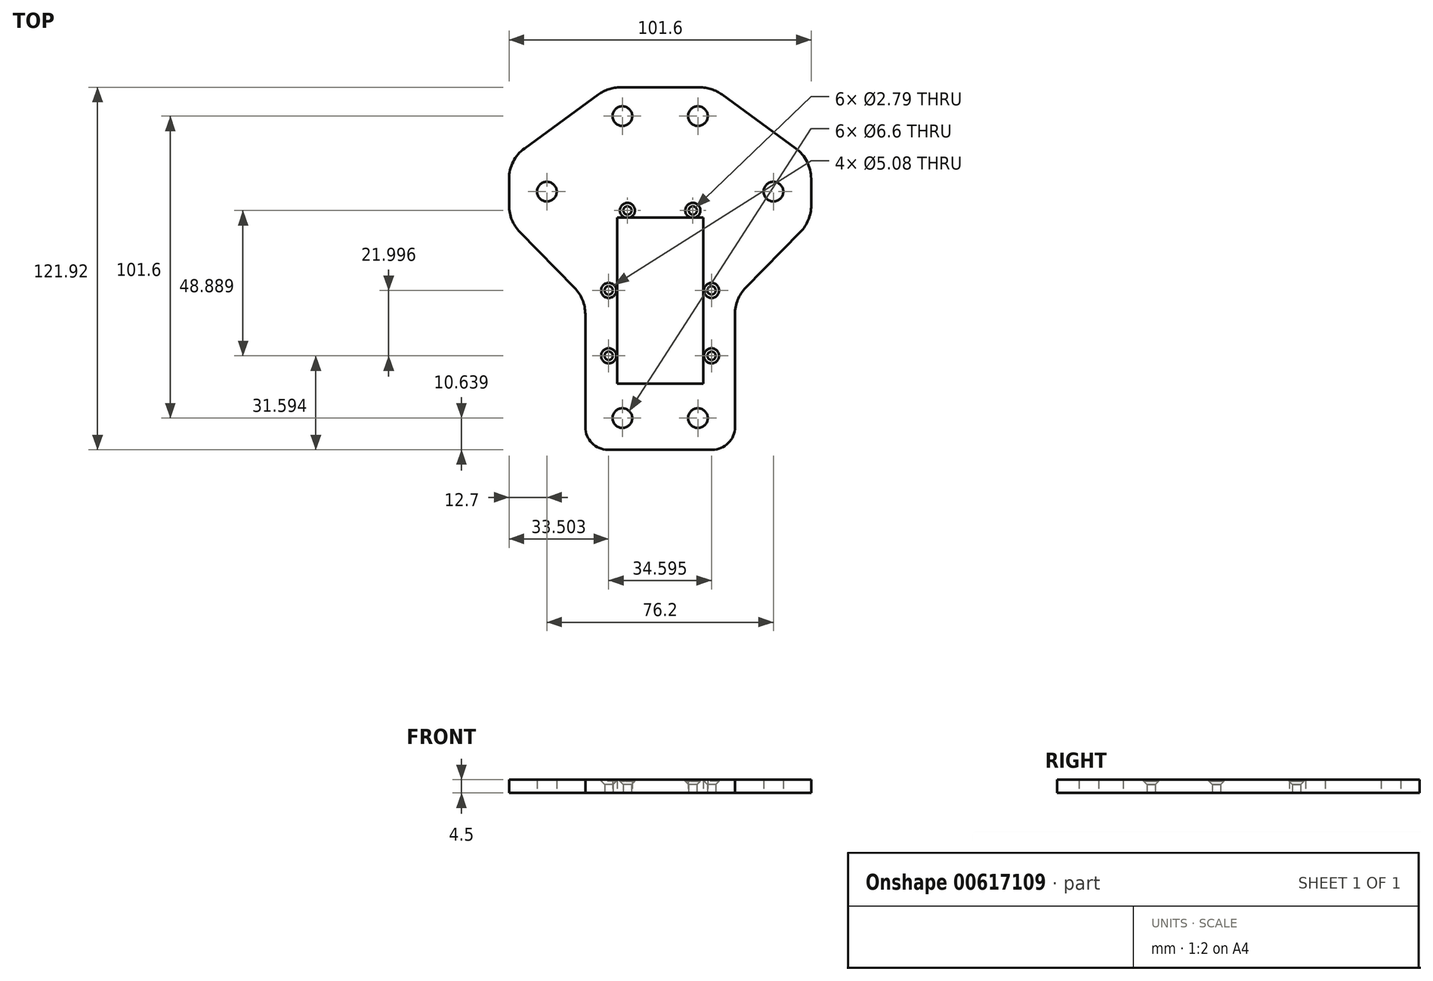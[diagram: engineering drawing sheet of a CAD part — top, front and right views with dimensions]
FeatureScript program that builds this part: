
annotation { "Feature Type Name" : "Feature", "Feature Type Description" : "" }
export const myFeature = defineFeature(function(context is Context, id is Id, definition is map)
    precondition{}
    {
        {
            var Q0;
            Q0=qCreatedBy(makeId("Top.planeOp"),FACE);
            var sketch = newSketch(context, id + "F0", { "sketchPlane" : qUnion([Q0])});
            skLineSegment(sketch, "E0", {"start": v(-13.32, 71.76) * mm, "end": v(0, 71.76) * mm});
            skLineSegment(sketch, "E1", {"start": v(-20.8, 69.31) * mm, "end": v(-45.59, 51.23) * mm});
            skLineSegment(sketch, "E2", {"start": v(-50.8, 40.97) * mm, "end": v(-50.8, 31.97) * mm});
            skLineSegment(sketch, "E3", {"start": v(-47.17, 23.08) * mm, "end": v(-28.8, 4.34) * mm});
            skLineSegment(sketch, "E4", {"start": v(-25.17, -4.55) * mm, "end": v(-25.17, -42.54) * mm});
            skLineSegment(sketch, "E5", {"start": v(-17.55, -50.16) * mm, "end": v(0, -50.16) * mm});
            skLineSegment(sketch, "E6", {"start": v(0, -50.16) * mm, "end": v(0, -27.94) * mm});
            skLineSegment(sketch, "E7", {"start": v(0, -27.94) * mm, "end": v(-14.5, -27.94) * mm});
            skLineSegment(sketch, "E8", {"start": v(-14.5, -27.94) * mm, "end": v(-14.5, 27.94) * mm});
            skLineSegment(sketch, "E9", {"start": v(-14.5, 27.94) * mm, "end": v(0, 27.94) * mm});
            skLineSegment(sketch, "E10", {"start": v(0, 27.94) * mm, "end": v(0, 71.76) * mm});
            skPoint(sketch, "E11.visualSharp", {"position": v(-17.46, 71.76) * mm});
            skArc(sketch, "E11.filletArc", {"start": v(-13.32, 71.76) * mm, "mid": v(-17.26, 71.13) * mm, "end": v(-20.8, 69.31) * mm});
            skPoint(sketch, "E12.visualSharp", {"position": v(-50.8, 47.42) * mm});
            skArc(sketch, "E12.filletArc", {"start": v(-45.59, 51.23) * mm, "mid": v(-49.42, 46.72) * mm, "end": v(-50.8, 40.97) * mm});
            skPoint(sketch, "E13.visualSharp", {"position": v(-50.8, 26.78) * mm});
            skArc(sketch, "E13.filletArc", {"start": v(-50.8, 31.97) * mm, "mid": v(-49.86, 27.17) * mm, "end": v(-47.17, 23.08) * mm});
            skPoint(sketch, "E14.visualSharp", {"position": v(-25.17, 0.64) * mm});
            skArc(sketch, "E14.filletArc", {"start": v(-25.17, -4.55) * mm, "mid": v(-26.11, 0.25) * mm, "end": v(-28.8, 4.34) * mm});
            skPoint(sketch, "E15.visualSharp", {"position": v(-25.17, -50.16) * mm});
            skArc(sketch, "E15.filletArc", {"start": v(-25.17, -42.54) * mm, "mid": v(-22.94, -47.93) * mm, "end": v(-17.55, -50.16) * mm});
            skLineSegment(sketch, "E16", {"start": v(-12.7, 83.28) * mm, "end": v(-12.7, -82.95) * mm, "construction": true});
            skLineSegment(sketch, "E17", {"start": v(91.24, 62.08) * mm, "end": v(-114.1, 62.08) * mm, "construction": true});
            skLineSegment(sketch, "E18", {"start": v(85.27, 36.68) * mm, "end": v(-111.23, 36.68) * mm, "construction": true});
            skLineSegment(sketch, "E19", {"start": v(-95.95, -39.52) * mm, "end": v(84.27, -39.52) * mm, "construction": true});
            skLineSegment(sketch, "E20", {"start": v(-38.1, 82.08) * mm, "end": v(-38.1, -58.2) * mm, "construction": true});
            skCircle(sketch, "E21", {"center": v(-12.7, 62.08) * mm, "radius": 3.3 * mm});
            skCircle(sketch, "E22", {"center": v(-38.1, 36.68) * mm, "radius": 3.3 * mm});
            skCircle(sketch, "E23", {"center": v(-12.7, -39.52) * mm, "radius": 3.3 * mm});
            skCircle(sketch, "E24", {"center": v(-11, 30.32) * mm, "radius": 1.4 * mm});
            skCircle(sketch, "E25", {"center": v(-17.3, 3.43) * mm, "radius": 1.4 * mm});
            skCircle(sketch, "E26", {"center": v(-17.3, -18.57) * mm, "radius": 1.4 * mm});
            skSolve(sketch);
        }
        {
            var Q0;
            Q0=makeQuery(id+"F0.imprint","IMPRINT",FACE,{"disambiguationData":[TD([[makeQuery(id+"F0.imprint","IMPRINT",EDGE,{"derivedFrom":sQuery(id+"F0.wireOp",EDGE,"E0")}),-1.0]])]});
            extrude(context, id + "F1", {"entities" : qUnion([Q0]), "depth" : 4.5 * mm, "offsetDistance" : 25.4 * mm});
        }
        {
            var Q0;
            Q0=makeQuery(id+"F1.opExtrude","SWEPT_BODY",BODY,{"disambiguationData":[OSD([sQuery(id+"F0.wireOp",EDGE,"E0"),sQuery(id+"F0.wireOp",EDGE,"E1"),sQuery(id+"F0.wireOp",EDGE,"E2"),sQuery(id+"F0.wireOp",EDGE,"E3"),sQuery(id+"F0.wireOp",EDGE,"E4"),sQuery(id+"F0.wireOp",EDGE,"E5"),sQuery(id+"F0.wireOp",EDGE,"E6"),sQuery(id+"F0.wireOp",EDGE,"E7"),sQuery(id+"F0.wireOp",EDGE,"E8"),sQuery(id+"F0.wireOp",EDGE,"E9"),sQuery(id+"F0.wireOp",EDGE,"E10"),sQuery(id+"F0.wireOp",EDGE,"E11.filletArc"),sQuery(id+"F0.wireOp",EDGE,"E12.filletArc"),sQuery(id+"F0.wireOp",EDGE,"E13.filletArc"),sQuery(id+"F0.wireOp",EDGE,"E14.filletArc"),sQuery(id+"F0.wireOp",EDGE,"E15.filletArc"),sQuery(id+"F0.wireOp",EDGE,"E21"),sQuery(id+"F0.wireOp",EDGE,"E22"),sQuery(id+"F0.wireOp",EDGE,"E23"),sQuery(id+"F0.wireOp",EDGE,"E24"),sQuery(id+"F0.wireOp",EDGE,"E25"),sQuery(id+"F0.wireOp",EDGE,"E26")])]});
            var Q1;
            Q1=makeQuery(id+"F1.opExtrude","SWEPT_FACE",FACE,{"disambiguationData":[OSD([sQuery(id+"F0.wireOp",EDGE,"E10")])]});
            mirror(context, id + "F2", {"operationType" : NewBodyOperationType.ADD, "entities" : qUnion([Q0]), "mirrorPlane" : qUnion([Q1])});
        }
        {
            var Q0;
            {var subQ0=makeQuery(id+"F1.opExtrude","CAP_FACE",FACE,{"disambiguationData":[OSD([sQuery(id+"F0.wireOp",EDGE,"E0"),sQuery(id+"F0.wireOp",EDGE,"E1"),sQuery(id+"F0.wireOp",EDGE,"E2"),sQuery(id+"F0.wireOp",EDGE,"E3"),sQuery(id+"F0.wireOp",EDGE,"E4"),sQuery(id+"F0.wireOp",EDGE,"E5"),sQuery(id+"F0.wireOp",EDGE,"E6"),sQuery(id+"F0.wireOp",EDGE,"E7"),sQuery(id+"F0.wireOp",EDGE,"E8"),sQuery(id+"F0.wireOp",EDGE,"E9"),sQuery(id+"F0.wireOp",EDGE,"E10"),sQuery(id+"F0.wireOp",EDGE,"E11.filletArc"),sQuery(id+"F0.wireOp",EDGE,"E12.filletArc"),sQuery(id+"F0.wireOp",EDGE,"E13.filletArc"),sQuery(id+"F0.wireOp",EDGE,"E14.filletArc"),sQuery(id+"F0.wireOp",EDGE,"E15.filletArc"),sQuery(id+"F0.wireOp",EDGE,"E21"),sQuery(id+"F0.wireOp",EDGE,"E22"),sQuery(id+"F0.wireOp",EDGE,"E23"),sQuery(id+"F0.wireOp",EDGE,"E24"),sQuery(id+"F0.wireOp",EDGE,"E25"),sQuery(id+"F0.wireOp",EDGE,"E26")])],"isStart":false});Q0=makeQuery(id+"F2.boolean.opBoolean","MERGE",FACE,{"derivedFrom":[subQ0,makeQuery(id+"F2.opPattern","COPY",FACE,{"derivedFrom":subQ0,"instanceName":"1"})]});}
            var sketch = newSketch(context, id + "F3", { "sketchPlane" : qUnion([Q0])});
            skCircle(sketch, "E27", {"center": v(-11, 30.32) * mm, "radius": 2.54 * mm});
            skCircle(sketch, "E28", {"center": v(-17.3, 3.43) * mm, "radius": 2.54 * mm});
            skCircle(sketch, "E29", {"center": v(-17.3, -18.57) * mm, "radius": 2.54 * mm});
            skCircle(sketch, "E30", {"center": v(11, 30.32) * mm, "radius": 2.54 * mm});
            skCircle(sketch, "E31", {"center": v(17.3, 3.43) * mm, "radius": 2.54 * mm});
            skCircle(sketch, "E32", {"center": v(17.3, -18.57) * mm, "radius": 2.54 * mm});
            skSolve(sketch);
        }
        {
            var Q0;
            Q0=qSketchRegion(id+"F3",true);
            extrude(context, id + "F4", {"entities" : qUnion([Q0]), "operationType" : NewBodyOperationType.REMOVE, "oppositeDirection" : true, "depth" : 0.38 * mm, "offsetDistance" : 25.4 * mm});
        }
        {
            var Q0;
            Q0=makeQuery(id+"F4.boolean.opBoolean","INTERSECT",EDGE,{"derivedFrom":[makeQuery(id+"F1.opExtrude","SWEPT_FACE",FACE,{"disambiguationData":[OSD([sQuery(id+"F0.wireOp",EDGE,"E24")])]}),makeQuery(id+"F4.opExtrude","CAP_FACE",FACE,{"disambiguationData":[OSD([sQuery(id+"F3.wireOp",EDGE,"E27")])],"isStart":false})]});
            var Q1;
            Q1=makeQuery(id+"F4.boolean.opBoolean","INTERSECT",EDGE,{"derivedFrom":[makeQuery(id+"F2.opPattern","COPY",FACE,{"derivedFrom":makeQuery(id+"F1.opExtrude","SWEPT_FACE",FACE,{"disambiguationData":[OSD([sQuery(id+"F0.wireOp",EDGE,"E24")])]}),"instanceName":"1"}),makeQuery(id+"F4.opExtrude","CAP_FACE",FACE,{"disambiguationData":[OSD([sQuery(id+"F3.wireOp",EDGE,"E30")])],"isStart":false})]});
            var Q2;
            Q2=makeQuery(id+"F4.boolean.opBoolean","INTERSECT",EDGE,{"derivedFrom":[makeQuery(id+"F1.opExtrude","SWEPT_FACE",FACE,{"disambiguationData":[OSD([sQuery(id+"F0.wireOp",EDGE,"E25")])]}),makeQuery(id+"F4.opExtrude","CAP_FACE",FACE,{"disambiguationData":[OSD([sQuery(id+"F3.wireOp",EDGE,"E28")])],"isStart":false})]});
            var Q3;
            Q3=makeQuery(id+"F4.boolean.opBoolean","INTERSECT",EDGE,{"derivedFrom":[makeQuery(id+"F2.opPattern","COPY",FACE,{"derivedFrom":makeQuery(id+"F1.opExtrude","SWEPT_FACE",FACE,{"disambiguationData":[OSD([sQuery(id+"F0.wireOp",EDGE,"E25")])]}),"instanceName":"1"}),makeQuery(id+"F4.opExtrude","CAP_FACE",FACE,{"disambiguationData":[OSD([sQuery(id+"F3.wireOp",EDGE,"E31")])],"isStart":false})]});
            var Q4;
            Q4=makeQuery(id+"F4.boolean.opBoolean","INTERSECT",EDGE,{"derivedFrom":[makeQuery(id+"F1.opExtrude","SWEPT_FACE",FACE,{"disambiguationData":[OSD([sQuery(id+"F0.wireOp",EDGE,"E26")])]}),makeQuery(id+"F4.opExtrude","CAP_FACE",FACE,{"disambiguationData":[OSD([sQuery(id+"F3.wireOp",EDGE,"E29")])],"isStart":false})]});
            var Q5;
            Q5=makeQuery(id+"F4.boolean.opBoolean","INTERSECT",EDGE,{"derivedFrom":[makeQuery(id+"F2.opPattern","COPY",FACE,{"derivedFrom":makeQuery(id+"F1.opExtrude","SWEPT_FACE",FACE,{"disambiguationData":[OSD([sQuery(id+"F0.wireOp",EDGE,"E26")])]}),"instanceName":"1"}),makeQuery(id+"F4.opExtrude","CAP_FACE",FACE,{"disambiguationData":[OSD([sQuery(id+"F3.wireOp",EDGE,"E32")])],"isStart":false})]});
            chamfer(context, id + "F5", {"entities" : qUnion([Q0, Q1, Q2, Q3, Q4, Q5]), "width" : 1.27 * mm, "tangentPropagation" : true});
        }
    });
